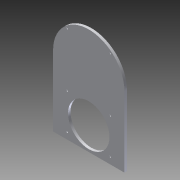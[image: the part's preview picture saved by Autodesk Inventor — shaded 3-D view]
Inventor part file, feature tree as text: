
AUTODESK INVENTOR PART (.ipt)
format: ipt  version: 2011 SP1 (Build 150282100, 282)  size: 96,768 bytes
history: native  units: in
note: dims shown in document units (in); Inventor stores cm internally (conversion verified against a paired STEP export)
features: hole x7, extrude x1, sketch x1
ambient origin geometry x8: Origin, YZ Plane, XZ Plane, XY Plane, X Axis, Y Axis, Z Axis, Center Point
bodies: Solid1 (feature_tree)
feature tree (9):
  extrude  "Extrusion1"  Depth=16.0in
  hole  "Hole1"  [1 undecoded]
  hole  "Hole2"  [1 undecoded]
  hole  "Hole3"  [1 undecoded]
  hole  "Hole4"  [1 undecoded]
  hole  "Hole5"  [1 undecoded]
  hole  "Hole6"  [1 undecoded]
  hole  "Hole7"  [1 undecoded]
  sketch  "Sketch1"  dims[d0=10.75in d1=16.0in d2=0.375in d3=0.0in d4=2.125in d5=1.0in d6=0.25in d7=0.75in d8=0.375in d9=0.25in d10=0.5635in d11=1.0in d12=0.8108in d13=1.0in d14=2.125in d15=0.25in d16=0.75in d17=0.375in d18=0.25in d19=0.5635in d20=1.0in d21=0.8108in d22=2.125in d23=6.375in d24=0.25in d25=0.75in d26=0.375in d27=0.25in d28=0.5635in d29=1.0in d30=0.8108in d31=6.375in d32=2.125in d33=0.25in d34=0.75in d35=0.375in d36=0.25in d37=0.5635in d38=1.0in d39=0.8108in d40=2.125in d41=14.5in d42=0.25in d43=0.75in d44=0.375in d45=0.25in d46=0.5635in d47=1.0in d48=0.8108in d49=2.125in d50=14.5in d51=0.25in d52=0.75in d53=0.375in d54=0.25in d55=0.5635in d56=1.0in d57=0.8108in d58=3.5in d59=5.375in d60=6.25in d61=0.75in d62=0.375in d63=0.25in d64=0.5635in d65=1.0in d66=0.8108in]
note: 7 required parameter values undecoded (feature->parameter linkage not recoverable at this tier; creation-order binding heuristic only, values carry confidence <= 0.55)
